# Revit family: РадиаторОтопления_Панельный_Стальной_Тип33_OasisPRO_ForteHome 2
name_source: partatom
category: Оборудование
revit_build: Autodesk Revit 2017 (Build: 20170118_1100(x64)
units: mm (PartAtom-declared; Revit-internal decimal feet)

## family parameters
Всегда вертикально = Да
На основе рабочей плоскости = Нет
Общий = Нет
При загрузке вырезать с полостями = Нет
Размер круглого соединителя = Использовать диаметр
Тип детали = Нормальный
Точка расчета площади = Нет

## types (6) — shared parameters
ADSK_Единица измерения = шт
ADSK_Завод-изготовитель = Forte Home - Россия
ADSK_Обозначение = ГОСТ 31311-2005
Глубина = 157 мм
ДиагональПодключение_ПодачаСлева = ДиагональПодключение_ПодачаСлева
ДиагональПодключение_ПодачаСправа = ДиагональПодключение_ПодачаСправа
ЛевБокПодключение_ПодачаСверху = ЛевБокПодключение_ПодачаСверху
ЛевБокПодключение_ПодачаСнизу = ЛевБокПодключение_ПодачаСнизу
НижнеБокПодключение_ПодачаСлева = НижнеБокПодключение_ПодачаСлева
НижнеБокПодключение_ПодачаСправа = НижнеБокПодключение_ПодачаСправа
ОтСтеныДоЗаднейПлоскости = 32 мм
ОтСтеныДоПлоскостиПодключения = 83 мм
ПравБокПодключение_ПодачаСверху = ПравБокПодключение_ПодачаСверху
ПравБокПодключение_ПодачаСнизу = ПравБокПодключение_ПодачаСнизу
Тип = 33

## per-type parameters (varying)
| type | Patrubki | Высота | ТипРадиатора300мм | ТипРадиатора500мм | ТипРадиатораБезНижнихПатрубков | ТипРадиатораСНижнимиПатрубкамиСлева | ТипРадиатораСНижнимиПатрубкамиСправа |
| PN-33-3-... (правый по умолчанию) радиатор с нижними патрубками справа, высота 300мм | 1 | 300 мм | Да | Нет | Нет | Нет | Да |
| PN-33-3-...(л) (левый под заказ) радиатор с нижними патрубками слева, высота 300мм | 2 | 300 мм | Да | Нет | Нет | Да | Нет |
| PN-33-5-... (правый по умолчанию) радиатор с нижними патрубками справа, высота 500мм | 1 | 500 мм | Нет | Да | Нет | Нет | Да |
| PN-33-5...(л) (левый под заказ) радиатор с нижними патрубками слева, высота 500мм | 2 | 500 мм | Нет | Да | Нет | Да | Нет |
| PB-33-5-... радиатор без нижних патрубков, высота 500мм | 3 | 500 мм | Нет | Да | Да | Нет | Нет |
| PB-33-3-... радиатор без нижних патрубков, высота 300мм | 3 | 300 мм | Да | Нет | Да | Нет | Нет |
